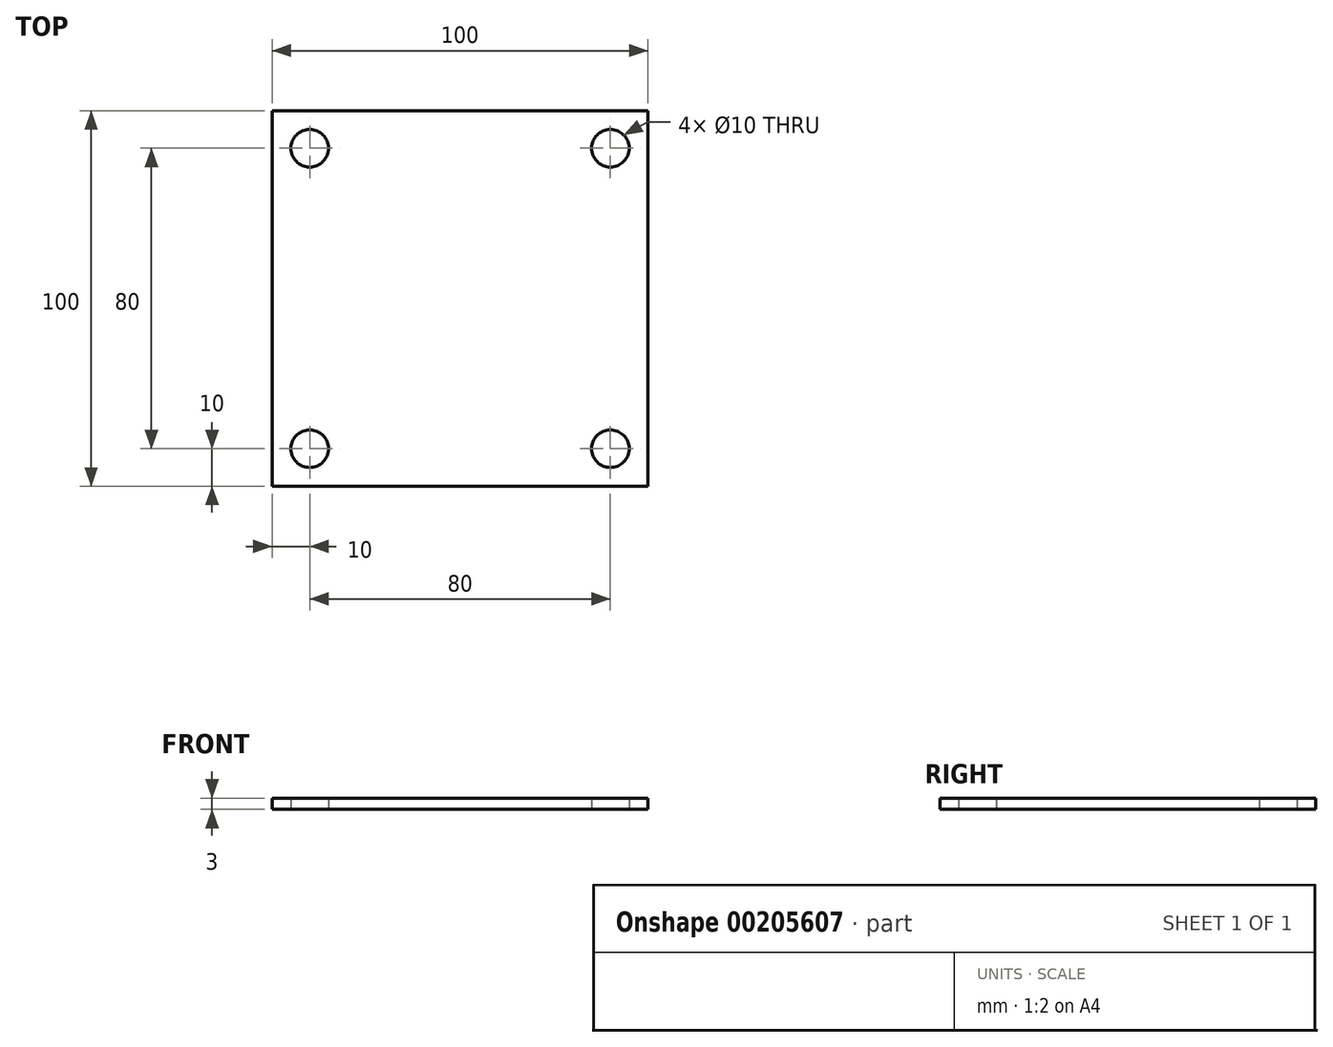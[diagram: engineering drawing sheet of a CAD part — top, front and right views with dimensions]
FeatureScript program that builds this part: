
annotation { "Feature Type Name" : "Feature", "Feature Type Description" : "" }
export const myFeature = defineFeature(function(context is Context, id is Id, definition is map)
    precondition{}
    {
        {
            var Q0;
            Q0=qCreatedBy(makeId("Top.planeOp"),FACE);
            var sketch = newSketch(context, id + "F0", { "sketchPlane" : qUnion([Q0])});
            skLineSegment(sketch, "E0.bottom", {"start": v(50, -50) * mm, "end": v(-50, -50) * mm});
            skLineSegment(sketch, "E0.top", {"start": v(50, 50) * mm, "end": v(-50, 50) * mm});
            skLineSegment(sketch, "E0.left", {"start": v(50, -50) * mm, "end": v(50, 50) * mm});
            skLineSegment(sketch, "E0.right", {"start": v(-50, -50) * mm, "end": v(-50, 50) * mm});
            skPoint(sketch, "E0.middle", {"position": v(0, 0) * mm});
            skSolve(sketch);
        }
        {
            var Q0;
            Q0 = qSketchRegion(id + "F0", true);
            extrude(context, id + "F1", {"entities" : qUnion([Q0]), "depth" : 3 * mm});
        }
        {
            var Q0;
            Q0=makeQuery(id+"F1.opExtrude","CAP_FACE",FACE,{"disambiguationData":[OSD([sQuery(id+"F0.wireOp",EDGE,"E0.bottom"),sQuery(id+"F0.wireOp",EDGE,"E0.top"),sQuery(id+"F0.wireOp",EDGE,"E0.left"),sQuery(id+"F0.wireOp",EDGE,"E0.right")])],"isStart":true});
            var sketch = newSketch(context, id + "F2", { "sketchPlane" : qUnion([Q0])});
            skCircle(sketch, "E1", {"center": v(40, 40) * mm, "radius": 5 * mm});
            skCircle(sketch, "E2", {"center": v(40, -40) * mm, "radius": 5 * mm});
            skCircle(sketch, "E3", {"center": v(-40, -40) * mm, "radius": 5 * mm});
            skCircle(sketch, "E4", {"center": v(-40, 40) * mm, "radius": 5 * mm});
            skSolve(sketch);
        }
        {
            var Q0;
            Q0 = qSketchRegion(id + "F2", true);
            extrude(context, id + "F3", {"entities" : qUnion([Q0]), "operationType" : NewBodyOperationType.REMOVE, "oppositeDirection" : true, "depth" : 25 * mm});
        }
        {
            var Q0;
            Q0=makeQuery(id+"F1.opExtrude","CAP_FACE",FACE,{"disambiguationData":[OSD([sQuery(id+"F0.wireOp",EDGE,"E0.bottom"),sQuery(id+"F0.wireOp",EDGE,"E0.top"),sQuery(id+"F0.wireOp",EDGE,"E0.left"),sQuery(id+"F0.wireOp",EDGE,"E0.right")])],"isStart":true});
            var sketch = newSketch(context, id + "F4", { "sketchPlane" : qUnion([Q0])});
            skCircle(sketch, "E5", {"center": v(10.68, 0) * mm, "radius": 4 * mm});
            skLineSegment(sketch, "E6", {"start": v(0, 0) * mm, "end": v(0, 10.73) * mm, "construction": true});
            skSolve(sketch);
        }
        {
            var Q0;
            Q0=sQuery(id+"F4.wireOp",EDGE,"E5");
            var Q1;
            Q1=sQuery(id+"F4.wireOp",EDGE,"E6");
            revolve(context, id + "F5", {"bodyType" : ToolBodyType.SURFACE, "surfaceEntities" : qUnion([Q0]), "axis" : qUnion([Q1]), "revolveType" : RevolveType.ONE_DIRECTION, "oppositeDirection" : true, "angle" : 180 * degree});
        }
    });
